# Revit family: BIG_MAX_O
name_source: partatom
category: Plumbing Fixtures
units: mm (PartAtom-declared; Revit-internal decimal feet)

## family parameters
Always vertical = Yes
Classification Number = 23.45.00.00
Cut with Voids When Loaded = Yes
Enable Cutting in Views = No
Maintain Annotation Orientation = No
Part Type = Normal
Room Calculation Point = No
Round Connector Dimension = Use Diameter
Shared = No
Work Plane-Based = No

## types (3) — shared parameters
Default Elevation = 0"
Manufacturer = MIFAB
Material = Polyethylene, High Density
Vesibility-Vent = Yes
array = 2

## per-type parameters (varying)
- BIG-1150-O: Description=300 gal/ft3 Big Max HDPE Oil Interceptor; Ext End=-20"; Front Extude=27 1/2"; Height of Body=50"; Length=83"; Lid Height from Inlet/Outlet Center (15.5" Min. thru 24.5" Max.)=24 1/4"; Model=XL-MI-G-PL-1150; Oil Draw off=4 1/32"; Pipe RP=38"; Top RP 1=19"; Top vent=9 7/16"; URL=www,mifab.com; Vent=40"; Vent Pipe=0"; Vent/2=20"; Visibility-1=No; Visiblity=Yes; Void 1 H=7"; Void 1 L=14"; Void 1 TL=12"; Width=33 1/2"; center void=10"; center void h=4 1/4"; pipe height=12 1/2"; v1=No; v2=Yes
- BIG-750-O: Description=140 gal/ft3 Big Max HDPE 750 Interceptor; Ext End=-16"; Front Extude=20 3/4"; Height of Body=37"; Length=50"; Lid Height from Inlet/Outlet Center (15.5" Min. thru 24.5" Max.)=24 1/4"; Model=XL-MI-G-PL-750; Oil Draw off=4 31/32"; Pipe RP=25 1/2"; Top RP 1=14"; Top vent=12 3/16"; URL=www.mifab.com; Vent=22"; Vent Pipe=3 3/16"; Vent/2=11"; Visibility-1=No; Visiblity=Yes; Void 1 H=4"; Void 1 L=7"; Void 1 TL=8"; Width=33 1/2"; center void=2"; center void h=2"; pipe height=12 3/4"; v1=Yes; v2=No
- BIG-500-O: Description=55 gal/ft3 Big Max HDPE Oil Interceptor
gallons.; Ext End=-12"; Front Extude=13 1/2"; Height of Body=26"; Length=37"; Lid Height from Inlet/Outlet Center (15.5" Min. thru 24.5" Max.)=24 1/2"; Model=XL-MI-G-PL-500; Oil Draw off=5 9/32"; Pipe RP=13 1/2"; Top RP 1=9"; Top vent=9 7/16"; URL=www.mifab.com; Vent=20"; Vent Pipe=0"; Vent/2=10"; Visibility-1=Yes; Visiblity=No; Void 1 H=3"; Void 1 L=3"; Void 1 TL=6"; Width=28"; center void=2"; center void h=2"; pipe height=12 3/4"; v1=No; v2=No

## geometry (parser evidence)
native form markers: Sweep x10
no freeform markers — native parametric forms only
